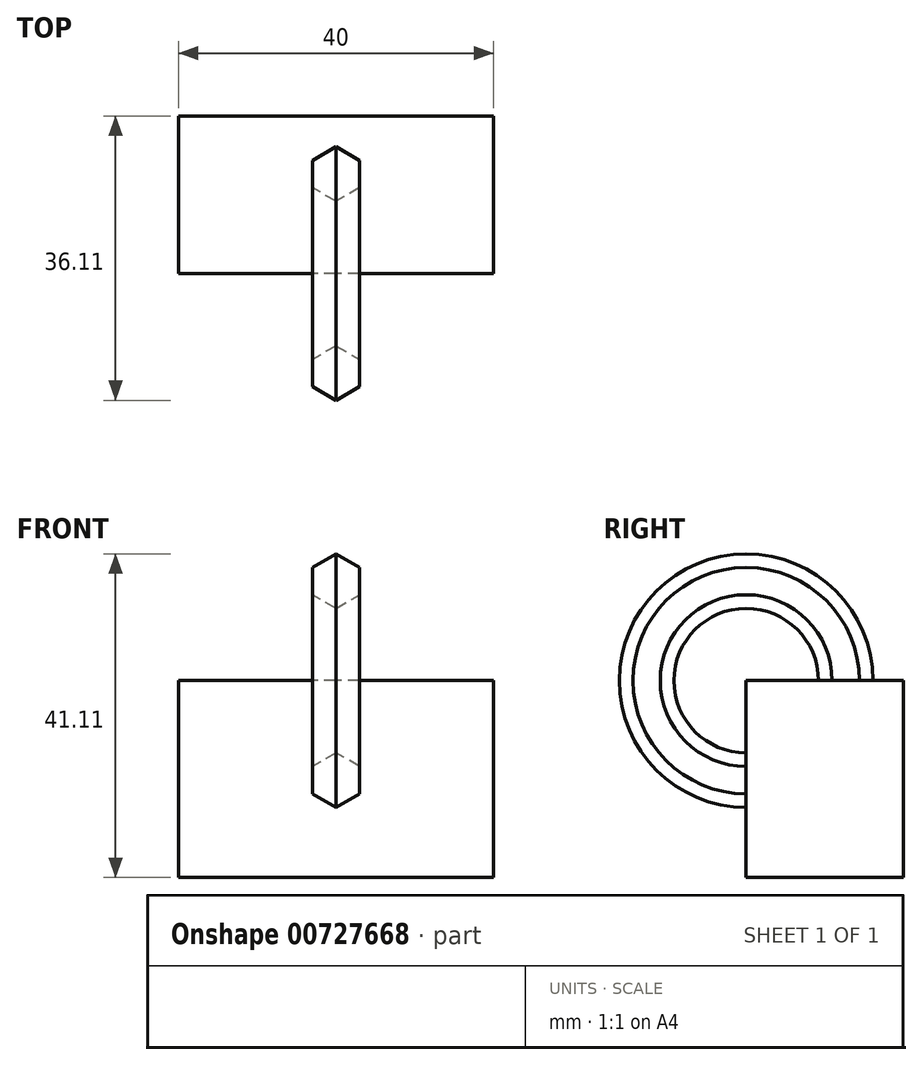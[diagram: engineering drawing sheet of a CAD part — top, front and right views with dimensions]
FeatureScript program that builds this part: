
annotation { "Feature Type Name" : "Feature", "Feature Type Description" : "" }
export const myFeature = defineFeature(function(context is Context, id is Id, definition is map)
    precondition{}
    {
        {
            var Q0;
            Q0=qCreatedBy(makeId("Top.planeOp"),FACE);
            var sketch = newSketch(context, id + "F0", { "sketchPlane" : qUnion([Q0])});
            skLineSegment(sketch, "E0.bottom", {"start": v(-94.3, 43.52) * mm, "end": v(-54.3, 43.52) * mm});
            skLineSegment(sketch, "E0.top", {"start": v(-94.3, 23.52) * mm, "end": v(-54.3, 23.52) * mm});
            skLineSegment(sketch, "E0.left", {"start": v(-94.3, 43.52) * mm, "end": v(-94.3, 23.52) * mm});
            skLineSegment(sketch, "E0.right", {"start": v(-54.3, 43.52) * mm, "end": v(-54.3, 23.52) * mm});
            skSolve(sketch);
        }
        {
            var Q0;
            Q0=makeQuery(id+"F0.imprint","IMPRINT",FACE,{"disambiguationData":[TD([[makeQuery(id+"F0.imprint","IMPRINT",EDGE,{"derivedFrom":sQuery(id+"F0.wireOp",EDGE,"E0.bottom")}),-1.0]])]});
            extrude(context, id + "F1", {"entities" : qUnion([Q0]), "depth" : 25 * mm, "offsetDistance" : 25 * mm});
        }
        {
            var Q0;
            Q0=makeQuery(id+"F1.opExtrude","CAP_FACE",FACE,{"disambiguationData":[OSD([sQuery(id+"F0.wireOp",EDGE,"E0.bottom"),sQuery(id+"F0.wireOp",EDGE,"E0.top"),sQuery(id+"F0.wireOp",EDGE,"E0.left"),sQuery(id+"F0.wireOp",EDGE,"E0.right")])],"isStart":false});
            var sketch = newSketch(context, id + "F2", { "sketchPlane" : qUnion([Q0])});
            skCircle(sketch, "E1.cCircle", {"center": v(-74.3, 36.16) * mm, "radius": 3 * mm, "construction": true});
            skPoint(sketch, "E1.cCircle.perimeterSnap0", {"position": v(-74.3, 43.52) * mm});
            skLineSegment(sketch, "E1.0", {"start": v(-74.3, 39.62) * mm, "end": v(-71.3, 37.9) * mm});
            skLineSegment(sketch, "E1.1", {"start": v(-71.3, 37.9) * mm, "end": v(-71.3, 34.43) * mm});
            skLineSegment(sketch, "E1.2", {"start": v(-71.3, 34.43) * mm, "end": v(-74.3, 32.7) * mm});
            skLineSegment(sketch, "E1.3", {"start": v(-74.3, 32.7) * mm, "end": v(-77.3, 34.43) * mm});
            skLineSegment(sketch, "E1.4", {"start": v(-77.3, 34.43) * mm, "end": v(-77.3, 37.9) * mm});
            skLineSegment(sketch, "E1.5", {"start": v(-77.3, 37.9) * mm, "end": v(-74.3, 39.62) * mm});
            skPoint(sketch, "E1.0.midPoint.positionSnap0", {"position": v(-74.3, 43.52) * mm});
            skPoint(sketch, "E2", {"position": v(-74.3, 23.52) * mm});
            skSolve(sketch);
        }
        {
            var Q0;
            Q0 = qSketchRegion(id + "F2", true);
            var Q1;
            Q1=makeQuery(id+"F1.opExtrude","CAP_EDGE",EDGE,{"disambiguationData":[OSD([sQuery(id+"F0.wireOp",EDGE,"E0.top")])],"isStart":false});
            revolve(context, id + "F3", {"operationType" : NewBodyOperationType.ADD, "surfaceOperationType" : NewSurfaceOperationType.NEW, "entities" : qUnion([Q0]), "axis" : qUnion([Q1]), "revolveType" : RevolveType.FULL});
        }
    });
